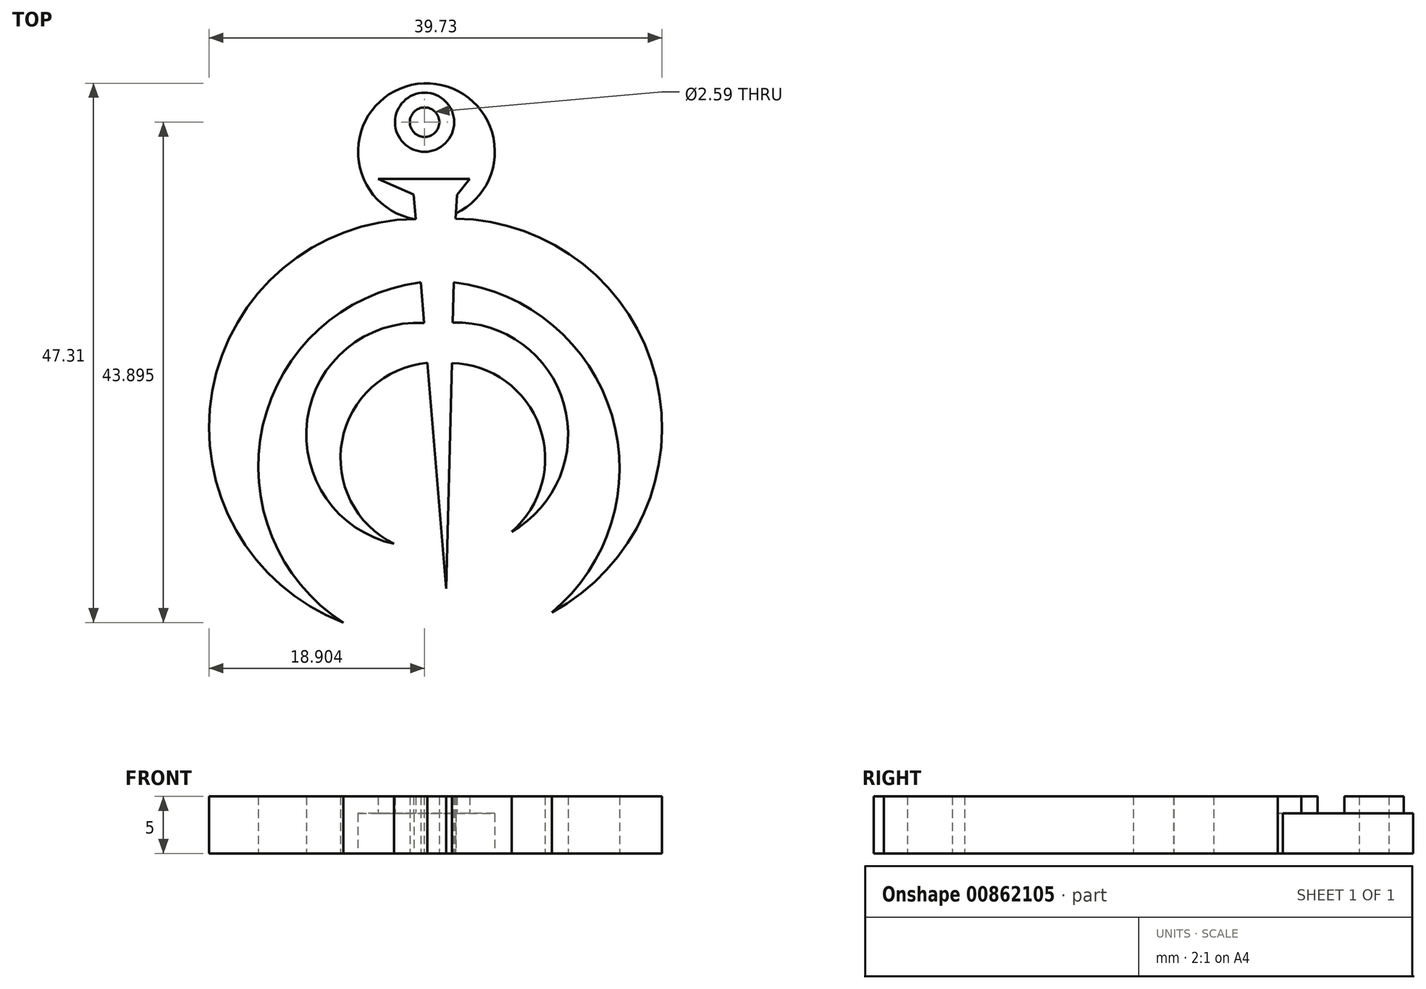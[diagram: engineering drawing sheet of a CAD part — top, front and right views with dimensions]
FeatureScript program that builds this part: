
annotation { "Feature Type Name" : "Feature", "Feature Type Description" : "" }
export const myFeature = defineFeature(function(context is Context, id is Id, definition is map)
    precondition{}
    {
        {
            var Q0;
            Q0=qCreatedBy(makeId("Top.planeOp"),FACE);
            var sketch = newSketch(context, id + "F0", { "sketchPlane" : qUnion([Q0])});
            skCircle(sketch, "E0", {"center": v(-2.52, 14.9) * mm, "radius": 2.6 * mm});
            skLineSegment(sketch, "E1", {"start": v(-6.59, 9.94) * mm, "end": v(1.43, 9.94) * mm});
            skLineSegment(sketch, "E2", {"start": v(1.43, 9.94) * mm, "end": v(0.32, 8.53) * mm});
            skArc(sketch, "E3", {"start": v(-3.3, 6.42) * mm, "mid": v(-21.13, -8.66) * mm, "end": v(-9.65, -29) * mm});
            skArc(sketch, "E4", {"start": v(8.64, -28.1) * mm, "mid": v(17.78, -7.56) * mm, "end": v(0.2, 6.45) * mm});
            skArc(sketch, "E5", {"start": v(-2.95, 0.83) * mm, "mid": v(-16.7, -11.74) * mm, "end": v(-9.65, -29) * mm});
            skArc(sketch, "E6", {"start": v(8.64, -28.1) * mm, "mid": v(13.9, -10.82) * mm, "end": v(0.1, 0.83) * mm});
            skLineSegment(sketch, "E7", {"start": v(-2.84, 0.85) * mm, "end": v(-2.55, -2.7) * mm});
            skLineSegment(sketch, "E8", {"start": v(0.05, 0.84) * mm, "end": v(-0.04, -2.67) * mm});
            skLineSegment(sketch, "E9", {"start": v(-2.95, 0.83) * mm, "end": v(-2.84, 0.85) * mm});
            skLineSegment(sketch, "E10", {"start": v(0.1, 0.83) * mm, "end": v(0.05, 0.84) * mm});
            skLineSegment(sketch, "E11", {"start": v(0.32, 8.53) * mm, "end": v(0.2, 6.45) * mm});
            skLineSegment(sketch, "E12", {"start": v(-3.3, 6.42) * mm, "end": v(-3.47, 8.56) * mm});
            skLineSegment(sketch, "E13", {"start": v(-3.47, 8.56) * mm, "end": v(-6.59, 9.94) * mm});
            skArc(sketch, "E14", {"start": v(-2.55, -2.7) * mm, "mid": v(-12.8, -11.18) * mm, "end": v(-5.19, -22.09) * mm});
            skArc(sketch, "E15", {"start": v(-2.26, -6.2) * mm, "mid": v(-9.75, -13.04) * mm, "end": v(-5.19, -22.09) * mm});
            skArc(sketch, "E16", {"start": v(5.1, -21.02) * mm, "mid": v(9.7, -9.83) * mm, "end": v(-0.04, -2.67) * mm});
            skArc(sketch, "E17", {"start": v(5.1, -21.02) * mm, "mid": v(7.57, -11.82) * mm, "end": v(-0.13, -6.22) * mm});
            skLineSegment(sketch, "E18.trimOffspring", {"start": v(-2.26, -6.2) * mm, "end": v(-0.63, -26.01) * mm});
            skLineSegment(sketch, "E19.trimOffspring", {"start": v(-0.13, -6.22) * mm, "end": v(-0.63, -26.01) * mm});
            skCircle(sketch, "E20", {"center": v(-2.52, 14.9) * mm, "radius": 1.3 * mm});
            skArc(sketch, "E21", {"start": v(0.22, 6.9) * mm, "mid": v(-3.13, 18.27) * mm, "end": v(-3.46, 6.42) * mm});
            skSolve(sketch);
        }
        {
            var Q0;
            Q0=makeQuery(id+"F0.imprint","IMPRINT",FACE,{"disambiguationData":[TD([[makeQuery(id+"F0.imprint","IMPRINT",EDGE,{"derivedFrom":sQuery(id+"F0.wireOp",EDGE,"E1")}),-1.0]])]});
            var Q1;
            Q1=makeQuery(id+"F0.imprint","IMPRINT",FACE,{"disambiguationData":[TD([[makeQuery(id+"F0.imprint","IMPRINT",EDGE,{"derivedFrom":sQuery(id+"F0.wireOp",EDGE,"E0")}),1.0]])]});
            extrude(context, id + "F1", {"entities" : qUnion([Q0, Q1]), "depth" : 5 * mm, "offsetDistance" : 25 * mm});
        }
        {
            var Q0;
            Q0=makeQuery(id+"F0.imprint","IMPRINT",FACE,{"disambiguationData":[TD([[makeQuery(id+"F0.imprint","IMPRINT",EDGE,{"derivedFrom":sQuery(id+"F0.wireOp",EDGE,"E0")}),-1.0]])]});
            extrude(context, id + "F2", {"entities" : qUnion([Q0]), "operationType" : NewBodyOperationType.ADD, "depth" : 3.5 * mm, "offsetDistance" : 25 * mm});
        }
    });
